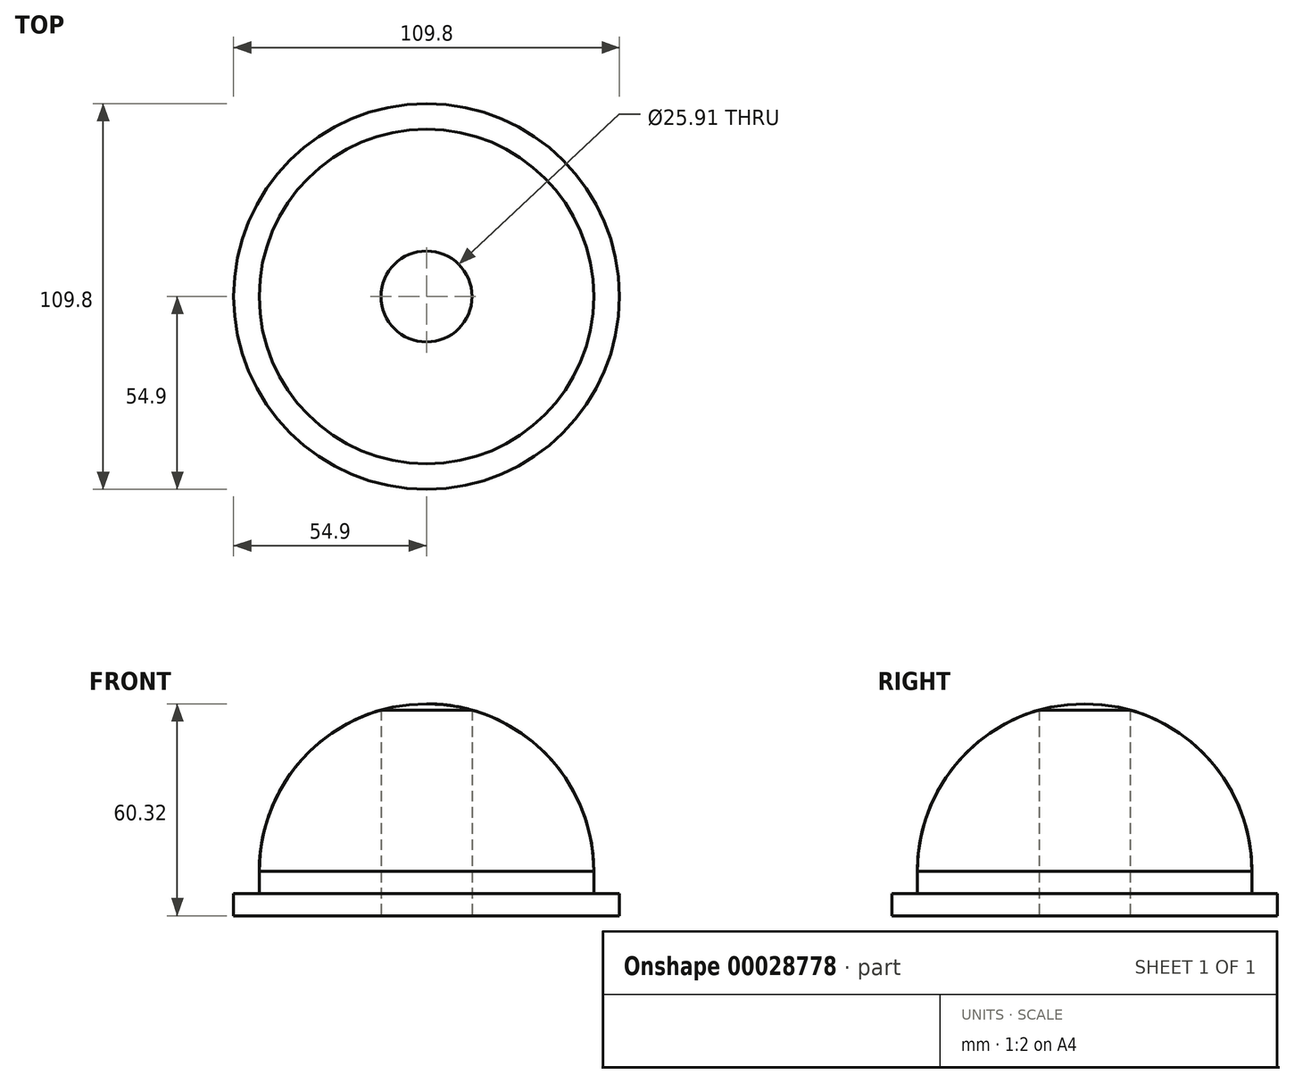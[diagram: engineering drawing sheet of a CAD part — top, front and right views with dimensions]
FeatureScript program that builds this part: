
annotation { "Feature Type Name" : "Feature", "Feature Type Description" : "" }
export const myFeature = defineFeature(function(context is Context, id is Id, definition is map)
    precondition{}
    {
        {
            var Q0;
            Q0=qCreatedBy(makeId("Front.planeOp"),FACE);
            var sketch = newSketch(context, id + "F0", { "sketchPlane" : qUnion([Q0])});
            skCircle(sketch, "E0", {"center": v(0, 0) * mm, "radius": 47.63 * mm});
            skLineSegment(sketch, "E1", {"start": v(-47.63, 0) * mm, "end": v(47.63, 0) * mm});
            skLineSegment(sketch, "E2.top", {"start": v(-47.63, -6.35) * mm, "end": v(47.63, -6.35) * mm});
            skLineSegment(sketch, "E2.left", {"start": v(-47.63, 0) * mm, "end": v(-47.63, -6.35) * mm});
            skLineSegment(sketch, "E2.right", {"start": v(47.63, 0) * mm, "end": v(47.63, -6.35) * mm});
            skLineSegment(sketch, "E3", {"start": v(0, 0) * mm, "end": v(0, 47.63) * mm});
            skLineSegment(sketch, "E4", {"start": v(0, 0) * mm, "end": v(0, -6.35) * mm});
            skLineSegment(sketch, "E5", {"start": v(-12.95, -6.35) * mm, "end": v(-12.95, 54.88) * mm});
            skLineSegment(sketch, "E6.bottom", {"start": v(-12.95, -6.35) * mm, "end": v(-54.9, -6.35) * mm});
            skLineSegment(sketch, "E6.top", {"start": v(-12.95, -12.7) * mm, "end": v(-54.9, -12.7) * mm});
            skLineSegment(sketch, "E6.left", {"start": v(-12.95, -6.35) * mm, "end": v(-12.95, -12.7) * mm});
            skLineSegment(sketch, "E6.right", {"start": v(-54.9, -6.35) * mm, "end": v(-54.9, -12.7) * mm});
            skSolve(sketch);
        }
        {
            var Q0;
            {var subQ3=sQuery(id+"F0.wireOp",EDGE,"E2.top");var subQ5=sQuery(id+"F0.wireOp",EDGE,"E5");var subQ6=makeQuery(id+"F0.imprint","INTERSECT",VERTEX,{"derivedFrom":[subQ3,subQ5]});Q0=makeQuery(id+"F0.imprint","IMPRINT",FACE,{"disambiguationData":[TD([[makeQuery(id+"F0.imprint","IMPRINT",EDGE,{"disambiguationData":[TD([[subQ6,1.0]])],"derivedFrom":subQ3}),1.0]])]});}
            var Q1;
            {var subQ1=sQuery(id+"F0.wireOp",EDGE,"E0");var subQ3=sQuery(id+"F0.wireOp",EDGE,"E5");var subQ4=makeQuery(id+"F0.imprint","INTERSECT",VERTEX,{"derivedFrom":[subQ1,subQ3]});Q1=makeQuery(id+"F0.imprint","IMPRINT",FACE,{"disambiguationData":[TD([[makeQuery(id+"F0.imprint","IMPRINT",EDGE,{"disambiguationData":[TD([[subQ4,1.0]])],"derivedFrom":subQ3}),1.0]])]});}
            var Q2;
            {var subQ1=sQuery(id+"F0.wireOp",EDGE,"E0");var subQ3=sQuery(id+"F0.wireOp",EDGE,"E6.bottom");var subQ4=makeQuery(id+"F0.imprint","INTERSECT",VERTEX,{"derivedFrom":[subQ1,subQ3]});Q2=makeQuery(id+"F0.imprint","IMPRINT",FACE,{"disambiguationData":[TD([[makeQuery(id+"F0.imprint","IMPRINT",EDGE,{"disambiguationData":[TD([[subQ4,1.0]])],"derivedFrom":subQ1}),1.0]])]});}
            var Q3;
            {var subQ5=sQuery(id+"F0.wireOp",EDGE,"E6.left");Q3=makeQuery(id+"F0.imprint","IMPRINT",FACE,{"disambiguationData":[TD([[makeQuery(id+"F0.imprint","IMPRINT",EDGE,{"derivedFrom":subQ5}),-1.0]])]});}
            var Q4;
            {var subQ0=sQuery(id+"F0.wireOp",EDGE,"E6.right");Q4=makeQuery(id+"F0.imprint","IMPRINT",FACE,{"disambiguationData":[TD([[makeQuery(id+"F0.imprint","IMPRINT",EDGE,{"derivedFrom":subQ0}),1.0]])]});}
            var Q5;
            {var subQ0=sQuery(id+"F0.wireOp",EDGE,"E2.left");Q5=makeQuery(id+"F0.imprint","IMPRINT",FACE,{"disambiguationData":[TD([[makeQuery(id+"F0.imprint","IMPRINT",EDGE,{"derivedFrom":subQ0}),1.0]])]});}
            var Q6;
            Q6=sQuery(id+"F0.wireOp",EDGE,"E3");
            revolve(context, id + "F1", {"entities" : qUnion([Q0, Q1, Q2, Q3, Q4, Q5]), "axis" : qUnion([Q6]), "revolveType" : RevolveType.FULL});
        }
    });
